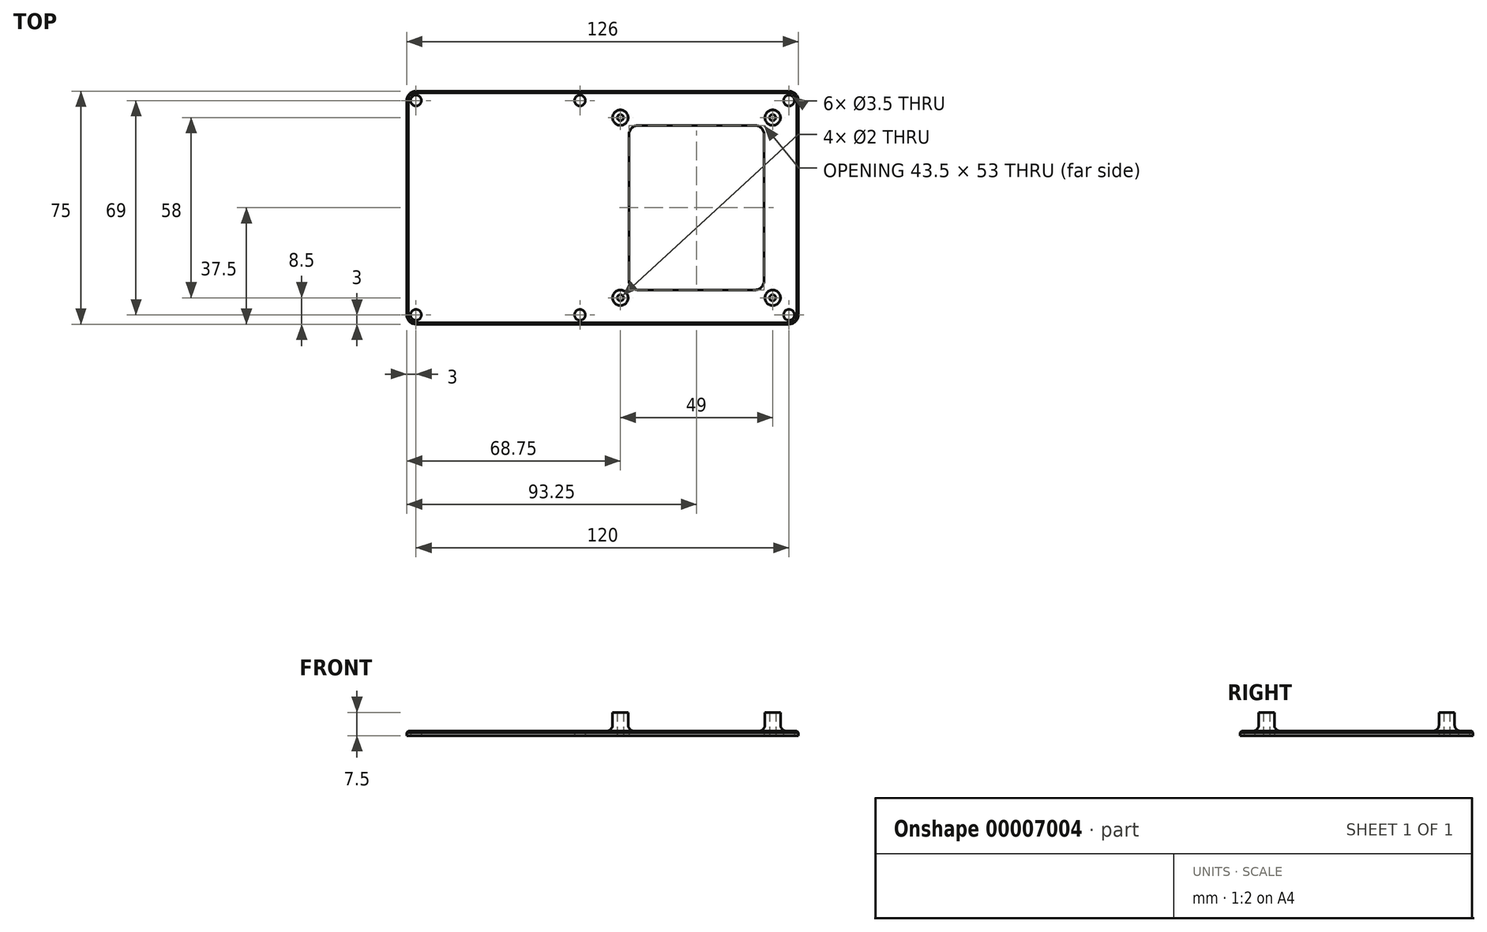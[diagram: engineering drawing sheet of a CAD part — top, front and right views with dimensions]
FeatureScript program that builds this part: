
annotation { "Feature Type Name" : "Feature", "Feature Type Description" : "" }
export const myFeature = defineFeature(function(context is Context, id is Id, definition is map)
    precondition{}
    {
        {
            var Q0;
            Q0=qCreatedBy(makeId("Top.planeOp"),FACE);
            var sketch = newSketch(context, id + "F0", { "sketchPlane" : qUnion([Q0])});
            skLineSegment(sketch, "E0", {"start": v(0, 0) * mm, "end": v(126, 0) * mm});
            skLineSegment(sketch, "E1", {"start": v(126, 0) * mm, "end": v(126, 75) * mm});
            skLineSegment(sketch, "E2", {"start": v(126, 75) * mm, "end": v(0, 75) * mm});
            skLineSegment(sketch, "E3", {"start": v(0, 75) * mm, "end": v(0, 0) * mm});
            skLineSegment(sketch, "E4", {"start": v(60.5, 75) * mm, "end": v(60.5, 0) * mm});
            skLineSegment(sketch, "E5.0", {"start": v(126, 64) * mm, "end": v(60.5, 64) * mm});
            skLineSegment(sketch, "E6.0", {"start": v(60.5, 11) * mm, "end": v(126, 11) * mm});
            skLineSegment(sketch, "E7.0", {"start": v(115, 0) * mm, "end": v(115, 75) * mm});
            skLineSegment(sketch, "E8", {"start": v(93.25, 75) * mm, "end": v(93.25, 0) * mm});
            skPoint(sketch, "E8.startSnap0", {"position": v(93.25, 64) * mm});
            skLineSegment(sketch, "E9", {"start": v(93.25, 37.5) * mm, "end": v(68.75, 37.5) * mm});
            skPoint(sketch, "E9.endSnap0", {"position": v(93.25, 37.5) * mm});
            skLineSegment(sketch, "E10", {"start": v(93.25, 37.5) * mm, "end": v(117.75, 37.5) * mm});
            skLineSegment(sketch, "E11", {"start": v(68.75, 37.5) * mm, "end": v(68.75, 66.5) * mm});
            skLineSegment(sketch, "E12", {"start": v(117.75, 37.5) * mm, "end": v(117.75, 8.5) * mm});
            skLineSegment(sketch, "E13.bottom", {"start": v(68.75, 66.5) * mm, "end": v(117.75, 66.5) * mm});
            skLineSegment(sketch, "E13.top", {"start": v(68.75, 8.5) * mm, "end": v(117.75, 8.5) * mm});
            skLineSegment(sketch, "E13.left", {"start": v(68.75, 66.5) * mm, "end": v(68.75, 8.5) * mm});
            skLineSegment(sketch, "E13.right", {"start": v(117.75, 66.5) * mm, "end": v(117.75, 8.5) * mm});
            skCircle(sketch, "E14", {"center": v(68.75, 8.5) * mm, "radius": 1 * mm});
            skCircle(sketch, "E15", {"center": v(117.75, 8.5) * mm, "radius": 1 * mm});
            skCircle(sketch, "E16", {"center": v(68.75, 66.5) * mm, "radius": 1 * mm});
            skCircle(sketch, "E17", {"center": v(117.75, 66.5) * mm, "radius": 1 * mm});
            skLineSegment(sketch, "E18.0", {"start": v(71.5, 75) * mm, "end": v(71.5, 0) * mm});
            skLineSegment(sketch, "E19", {"start": v(126, 37.5) * mm, "end": v(55.75, 37.5) * mm});
            skLineSegment(sketch, "E20", {"start": v(55.75, 37.5) * mm, "end": v(55.75, 72) * mm});
            skLineSegment(sketch, "E21", {"start": v(55.75, 37.5) * mm, "end": v(55.75, 3) * mm});
            skCircle(sketch, "E22", {"center": v(55.75, 3) * mm, "radius": 1.75 * mm});
            skCircle(sketch, "E23", {"center": v(55.75, 72) * mm, "radius": 1.75 * mm});
            skLineSegment(sketch, "E24.0", {"start": v(126, 72) * mm, "end": v(0, 72) * mm});
            skLineSegment(sketch, "E25.0", {"start": v(0, 3) * mm, "end": v(126, 3) * mm});
            skLineSegment(sketch, "E26.0", {"start": v(3, 75) * mm, "end": v(3, 0) * mm});
            skLineSegment(sketch, "E27.0", {"start": v(123, 0) * mm, "end": v(123, 75) * mm});
            skCircle(sketch, "E28", {"center": v(3, 3) * mm, "radius": 1.75 * mm});
            skCircle(sketch, "E29", {"center": v(123, 3) * mm, "radius": 1.75 * mm});
            skCircle(sketch, "E30", {"center": v(123, 72) * mm, "radius": 1.75 * mm});
            skCircle(sketch, "E31", {"center": v(3, 72) * mm, "radius": 1.75 * mm});
            skSolve(sketch);
        }
        {
            var Q0;
            Q0=qCreatedBy(makeId("Top.planeOp"),FACE);
            var sketch = newSketch(context, id + "F1", { "sketchPlane" : qUnion([Q0])});
            skLineSegment(sketch, "E32.0", {"start": v(0, 75) * mm, "end": v(0, 0) * mm});
            skLineSegment(sketch, "E32.1", {"start": v(126, 75) * mm, "end": v(0, 75) * mm});
            skLineSegment(sketch, "E32.2", {"start": v(126, 0) * mm, "end": v(126, 75) * mm});
            skLineSegment(sketch, "E32.3", {"start": v(0, 0) * mm, "end": v(126, 0) * mm});
            skCircle(sketch, "E32.4", {"center": v(55.75, 3) * mm, "radius": 1.75 * mm});
            skCircle(sketch, "E32.5", {"center": v(123, 3) * mm, "radius": 1.75 * mm});
            skCircle(sketch, "E32.6", {"center": v(55.75, 72) * mm, "radius": 1.75 * mm});
            skCircle(sketch, "E32.7", {"center": v(123, 72) * mm, "radius": 1.75 * mm});
            skLineSegment(sketch, "E32.8", {"start": v(115, 11) * mm, "end": v(115, 64) * mm});
            skLineSegment(sketch, "E32.9", {"start": v(115, 64) * mm, "end": v(71.5, 64) * mm});
            skLineSegment(sketch, "E32.10", {"start": v(71.5, 64) * mm, "end": v(71.5, 11) * mm});
            skLineSegment(sketch, "E32.11", {"start": v(71.5, 11) * mm, "end": v(115, 11) * mm});
            skCircle(sketch, "E32.12", {"center": v(3, 3) * mm, "radius": 1.75 * mm});
            skCircle(sketch, "E32.13", {"center": v(3, 72) * mm, "radius": 1.75 * mm});
            skPoint(sketch, "E33.orphan", {"position": v(60.5, 11) * mm});
            skPoint(sketch, "E34.orphan", {"position": v(71.5, 0) * mm});
            skPoint(sketch, "E35.orphan", {"position": v(60.5, 64) * mm});
            skPoint(sketch, "E36.orphan", {"position": v(71.5, 75) * mm});
            skPoint(sketch, "E37.orphan", {"position": v(115, 75) * mm});
            skPoint(sketch, "E38.orphan", {"position": v(126, 64) * mm});
            skPoint(sketch, "E39.orphan", {"position": v(126, 11) * mm});
            skPoint(sketch, "E40.orphan", {"position": v(115, 0) * mm});
            skSolve(sketch);
        }
        {
            var Q0;
            Q0 = qSketchRegion(id + "F1", true);
            extrude(context, id + "F2", {"entities" : qUnion([Q0]), "depth" : 1.5 * mm});
        }
        {
            var Q0;
            Q0=makeQuery(id+"F2.opExtrude","SWEPT_EDGE",EDGE,{"disambiguationData":[OSD([sQuery(id+"F1.wireOp",EDGE,"E32.0"),sQuery(id+"F1.wireOp",EDGE,"E32.3")])]});
            var Q1;
            Q1=makeQuery(id+"F2.opExtrude","SWEPT_EDGE",EDGE,{"disambiguationData":[OSD([sQuery(id+"F1.wireOp",EDGE,"E32.2"),sQuery(id+"F1.wireOp",EDGE,"E32.3")])]});
            var Q2;
            Q2=makeQuery(id+"F2.opExtrude","SWEPT_EDGE",EDGE,{"disambiguationData":[OSD([sQuery(id+"F1.wireOp",EDGE,"E32.0"),sQuery(id+"F1.wireOp",EDGE,"E32.1")])]});
            var Q3;
            Q3=makeQuery(id+"F2.opExtrude","SWEPT_EDGE",EDGE,{"disambiguationData":[OSD([sQuery(id+"F1.wireOp",EDGE,"E32.8"),sQuery(id+"F1.wireOp",EDGE,"E32.11")])]});
            var Q4;
            Q4=makeQuery(id+"F2.opExtrude","SWEPT_EDGE",EDGE,{"disambiguationData":[OSD([sQuery(id+"F1.wireOp",EDGE,"E32.9"),sQuery(id+"F1.wireOp",EDGE,"E32.10")])]});
            var Q5;
            Q5=makeQuery(id+"F2.opExtrude","SWEPT_EDGE",EDGE,{"disambiguationData":[OSD([sQuery(id+"F1.wireOp",EDGE,"E32.8"),sQuery(id+"F1.wireOp",EDGE,"E32.9")])]});
            var Q6;
            Q6=makeQuery(id+"F2.opExtrude","SWEPT_EDGE",EDGE,{"disambiguationData":[OSD([sQuery(id+"F1.wireOp",EDGE,"E32.1"),sQuery(id+"F1.wireOp",EDGE,"E32.2")])]});
            var Q7;
            Q7=makeQuery(id+"F2.opExtrude","SWEPT_EDGE",EDGE,{"disambiguationData":[OSD([sQuery(id+"F1.wireOp",EDGE,"E32.10"),sQuery(id+"F1.wireOp",EDGE,"E32.11")])]});
            fillet(context, id + "F3", {"entities" : qUnion([Q0, Q1, Q2, Q3, Q4, Q5, Q6, Q7]), "radius" : 3 * mm, "tangentPropagation" : true, "allowEdgeOverflow" : false});
        }
        {
            var Q0;
            Q0=qCreatedBy(makeId("Top.planeOp"),FACE);
            var sketch = newSketch(context, id + "F4", { "sketchPlane" : qUnion([Q0])});
            skCircle(sketch, "E41", {"center": v(68.75, 66.5) * mm, "radius": 2.5 * mm});
            skCircle(sketch, "E42", {"center": v(117.75, 66.5) * mm, "radius": 2.5 * mm});
            skCircle(sketch, "E43", {"center": v(68.75, 8.5) * mm, "radius": 2.5 * mm});
            skCircle(sketch, "E44", {"center": v(117.75, 8.5) * mm, "radius": 2.5 * mm});
            skSolve(sketch);
        }
        {
            var Q0;
            Q0 = qSketchRegion(id + "F4", true);
            extrude(context, id + "F5", {"entities" : qUnion([Q0]), "operationType" : NewBodyOperationType.ADD, "depth" : 7.5 * mm});
        }
        {
            var Q0;
            Q0=makeQuery(id+"F5.boolean.opBoolean","INTERSECT",EDGE,{"derivedFrom":[makeQuery(id+"F2.opExtrude","CAP_FACE",FACE,{"disambiguationData":[OSD([sQuery(id+"F1.wireOp",EDGE,"E32.0"),sQuery(id+"F1.wireOp",EDGE,"E32.1"),sQuery(id+"F1.wireOp",EDGE,"E32.2"),sQuery(id+"F1.wireOp",EDGE,"E32.3"),sQuery(id+"F1.wireOp",EDGE,"E32.4"),sQuery(id+"F1.wireOp",EDGE,"E32.5"),sQuery(id+"F1.wireOp",EDGE,"E32.6"),sQuery(id+"F1.wireOp",EDGE,"E32.7"),sQuery(id+"F1.wireOp",EDGE,"E32.8"),sQuery(id+"F1.wireOp",EDGE,"E32.9"),sQuery(id+"F1.wireOp",EDGE,"E32.10"),sQuery(id+"F1.wireOp",EDGE,"E32.11"),sQuery(id+"F1.wireOp",EDGE,"E32.12"),sQuery(id+"F1.wireOp",EDGE,"E32.13")])],"isStart":false}),makeQuery(id+"F5.opExtrude","SWEPT_FACE",FACE,{"disambiguationData":[OSD([sQuery(id+"F4.wireOp",EDGE,"E43")])]})]});
            var Q1;
            Q1=makeQuery(id+"F5.boolean.opBoolean","INTERSECT",EDGE,{"derivedFrom":[makeQuery(id+"F2.opExtrude","CAP_FACE",FACE,{"disambiguationData":[OSD([sQuery(id+"F1.wireOp",EDGE,"E32.0"),sQuery(id+"F1.wireOp",EDGE,"E32.1"),sQuery(id+"F1.wireOp",EDGE,"E32.2"),sQuery(id+"F1.wireOp",EDGE,"E32.3"),sQuery(id+"F1.wireOp",EDGE,"E32.4"),sQuery(id+"F1.wireOp",EDGE,"E32.5"),sQuery(id+"F1.wireOp",EDGE,"E32.6"),sQuery(id+"F1.wireOp",EDGE,"E32.7"),sQuery(id+"F1.wireOp",EDGE,"E32.8"),sQuery(id+"F1.wireOp",EDGE,"E32.9"),sQuery(id+"F1.wireOp",EDGE,"E32.10"),sQuery(id+"F1.wireOp",EDGE,"E32.11"),sQuery(id+"F1.wireOp",EDGE,"E32.12"),sQuery(id+"F1.wireOp",EDGE,"E32.13")])],"isStart":false}),makeQuery(id+"F5.opExtrude","SWEPT_FACE",FACE,{"disambiguationData":[OSD([sQuery(id+"F4.wireOp",EDGE,"E41")])]})]});
            var Q2;
            Q2=makeQuery(id+"F5.boolean.opBoolean","INTERSECT",EDGE,{"derivedFrom":[makeQuery(id+"F2.opExtrude","CAP_FACE",FACE,{"disambiguationData":[OSD([sQuery(id+"F1.wireOp",EDGE,"E32.0"),sQuery(id+"F1.wireOp",EDGE,"E32.1"),sQuery(id+"F1.wireOp",EDGE,"E32.2"),sQuery(id+"F1.wireOp",EDGE,"E32.3"),sQuery(id+"F1.wireOp",EDGE,"E32.4"),sQuery(id+"F1.wireOp",EDGE,"E32.5"),sQuery(id+"F1.wireOp",EDGE,"E32.6"),sQuery(id+"F1.wireOp",EDGE,"E32.7"),sQuery(id+"F1.wireOp",EDGE,"E32.8"),sQuery(id+"F1.wireOp",EDGE,"E32.9"),sQuery(id+"F1.wireOp",EDGE,"E32.10"),sQuery(id+"F1.wireOp",EDGE,"E32.11"),sQuery(id+"F1.wireOp",EDGE,"E32.12"),sQuery(id+"F1.wireOp",EDGE,"E32.13")])],"isStart":false}),makeQuery(id+"F5.opExtrude","SWEPT_FACE",FACE,{"disambiguationData":[OSD([sQuery(id+"F4.wireOp",EDGE,"E44")])]})]});
            var Q3;
            Q3=makeQuery(id+"F5.boolean.opBoolean","INTERSECT",EDGE,{"derivedFrom":[makeQuery(id+"F2.opExtrude","CAP_FACE",FACE,{"disambiguationData":[OSD([sQuery(id+"F1.wireOp",EDGE,"E32.0"),sQuery(id+"F1.wireOp",EDGE,"E32.1"),sQuery(id+"F1.wireOp",EDGE,"E32.2"),sQuery(id+"F1.wireOp",EDGE,"E32.3"),sQuery(id+"F1.wireOp",EDGE,"E32.4"),sQuery(id+"F1.wireOp",EDGE,"E32.5"),sQuery(id+"F1.wireOp",EDGE,"E32.6"),sQuery(id+"F1.wireOp",EDGE,"E32.7"),sQuery(id+"F1.wireOp",EDGE,"E32.8"),sQuery(id+"F1.wireOp",EDGE,"E32.9"),sQuery(id+"F1.wireOp",EDGE,"E32.10"),sQuery(id+"F1.wireOp",EDGE,"E32.11"),sQuery(id+"F1.wireOp",EDGE,"E32.12"),sQuery(id+"F1.wireOp",EDGE,"E32.13")])],"isStart":false}),makeQuery(id+"F5.opExtrude","SWEPT_FACE",FACE,{"disambiguationData":[OSD([sQuery(id+"F4.wireOp",EDGE,"E42")])]})]});
            fillet(context, id + "F6", {"entities" : qUnion([Q0, Q1, Q2, Q3]), "radius" : 2 * mm, "tangentPropagation" : true, "allowEdgeOverflow" : false});
        }
        {
            var Q0;
            {var subQ0=sQuery(id+"F0.wireOp",EDGE,"E13.left");var subQ1=sQuery(id+"F0.wireOp",EDGE,"E13.top");var subQ2=makeQuery(id+"F0.imprint","INTERSECT",VERTEX,{"derivedFrom":[subQ1,subQ0]});Q0=makeQuery(id+"F0.imprint","IMPRINT",FACE,{"disambiguationData":[TD([[makeQuery(id+"F0.imprint","IMPRINT",EDGE,{"disambiguationData":[TD([[subQ2,-1.0]])],"derivedFrom":subQ1}),-1.0]])]});}
            var Q1;
            {var subQ0=sQuery(id+"F0.wireOp",EDGE,"E13.left");var subQ1=sQuery(id+"F0.wireOp",EDGE,"E13.top");var subQ2=makeQuery(id+"F0.imprint","INTERSECT",VERTEX,{"derivedFrom":[subQ1,subQ0]});Q1=makeQuery(id+"F0.imprint","IMPRINT",FACE,{"disambiguationData":[TD([[makeQuery(id+"F0.imprint","IMPRINT",EDGE,{"disambiguationData":[TD([[subQ2,-1.0]])],"derivedFrom":subQ1}),1.0]])]});}
            var Q2;
            {var subQ0=sQuery(id+"F0.wireOp",EDGE,"E13.right");var subQ1=sQuery(id+"F0.wireOp",EDGE,"E13.top");var subQ2=makeQuery(id+"F0.imprint","INTERSECT",VERTEX,{"derivedFrom":[subQ1,subQ0]});Q2=makeQuery(id+"F0.imprint","IMPRINT",FACE,{"disambiguationData":[TD([[makeQuery(id+"F0.imprint","IMPRINT",EDGE,{"disambiguationData":[TD([[subQ2,1.0]])],"derivedFrom":subQ1}),-1.0]])]});}
            var Q3;
            {var subQ0=sQuery(id+"F0.wireOp",EDGE,"E13.right");var subQ1=sQuery(id+"F0.wireOp",EDGE,"E13.top");var subQ2=makeQuery(id+"F0.imprint","INTERSECT",VERTEX,{"derivedFrom":[subQ1,subQ0]});Q3=makeQuery(id+"F0.imprint","IMPRINT",FACE,{"disambiguationData":[TD([[makeQuery(id+"F0.imprint","IMPRINT",EDGE,{"disambiguationData":[TD([[subQ2,1.0]])],"derivedFrom":subQ1}),1.0]])]});}
            var Q4;
            {var subQ0=sQuery(id+"F0.wireOp",EDGE,"E13.right");var subQ1=sQuery(id+"F0.wireOp",EDGE,"E13.bottom");var subQ2=makeQuery(id+"F0.imprint","INTERSECT",VERTEX,{"derivedFrom":[subQ1,subQ0]});Q4=makeQuery(id+"F0.imprint","IMPRINT",FACE,{"disambiguationData":[TD([[makeQuery(id+"F0.imprint","IMPRINT",EDGE,{"disambiguationData":[TD([[subQ2,1.0]])],"derivedFrom":subQ1}),-1.0]])]});}
            var Q5;
            {var subQ0=sQuery(id+"F0.wireOp",EDGE,"E13.right");var subQ1=sQuery(id+"F0.wireOp",EDGE,"E13.bottom");var subQ2=makeQuery(id+"F0.imprint","INTERSECT",VERTEX,{"derivedFrom":[subQ1,subQ0]});Q5=makeQuery(id+"F0.imprint","IMPRINT",FACE,{"disambiguationData":[TD([[makeQuery(id+"F0.imprint","IMPRINT",EDGE,{"disambiguationData":[TD([[subQ2,1.0]])],"derivedFrom":subQ1}),1.0]])]});}
            var Q6;
            {var subQ0=sQuery(id+"F0.wireOp",EDGE,"E13.left");var subQ1=sQuery(id+"F0.wireOp",EDGE,"E13.bottom");var subQ2=makeQuery(id+"F0.imprint","INTERSECT",VERTEX,{"derivedFrom":[subQ1,subQ0]});Q6=makeQuery(id+"F0.imprint","IMPRINT",FACE,{"disambiguationData":[TD([[makeQuery(id+"F0.imprint","IMPRINT",EDGE,{"disambiguationData":[TD([[subQ2,-1.0]])],"derivedFrom":subQ1}),1.0]])]});}
            var Q7;
            {var subQ0=sQuery(id+"F0.wireOp",EDGE,"E13.left");var subQ1=sQuery(id+"F0.wireOp",EDGE,"E13.bottom");var subQ2=makeQuery(id+"F0.imprint","INTERSECT",VERTEX,{"derivedFrom":[subQ1,subQ0]});Q7=makeQuery(id+"F0.imprint","IMPRINT",FACE,{"disambiguationData":[TD([[makeQuery(id+"F0.imprint","IMPRINT",EDGE,{"disambiguationData":[TD([[subQ2,-1.0]])],"derivedFrom":subQ1}),-1.0]])]});}
            var Q8;
            Q8=sQuery(id+"F0.wireOp",EDGE,"E14");
            var Q9;
            Q9=sQuery(id+"F0.wireOp",EDGE,"E16");
            var Q10;
            Q10=sQuery(id+"F0.wireOp",EDGE,"E17");
            var Q11;
            Q11=sQuery(id+"F0.wireOp",EDGE,"E15");
            extrude(context, id + "F7", {"entities" : qUnion([Q0, Q1, Q2, Q3, Q4, Q5, Q6, Q7]), "operationType" : NewBodyOperationType.REMOVE, "surfaceEntities" : qUnion([Q8, Q9, Q10, Q11]), "depth" : 25 * mm});
        }
        {
            var Q0;
            Q0=makeQuery(id+"F2.opExtrude","CAP_EDGE",EDGE,{"disambiguationData":[OSD([sQuery(id+"F1.wireOp",EDGE,"E32.2")])],"isStart":false});
            var Q1;
            {var subQ0=sQuery(id+"F1.wireOp",EDGE,"E32.3");var subQ1=sQuery(id+"F1.wireOp",EDGE,"E32.2");Q1=makeQuery(id+"F3.opFillet","BLEND_EDGE",EDGE,{"blendedFrom":[makeQuery(id+"F2.opExtrude","SWEPT_EDGE",EDGE,{"disambiguationData":[OSD([subQ1,subQ0])]}),makeQuery(id+"F2.opExtrude","CAP_FACE",FACE,{"disambiguationData":[OSD([sQuery(id+"F1.wireOp",EDGE,"E32.0"),sQuery(id+"F1.wireOp",EDGE,"E32.1"),subQ1,subQ0,sQuery(id+"F1.wireOp",EDGE,"E32.4"),sQuery(id+"F1.wireOp",EDGE,"E32.5"),sQuery(id+"F1.wireOp",EDGE,"E32.6"),sQuery(id+"F1.wireOp",EDGE,"E32.7"),sQuery(id+"F1.wireOp",EDGE,"E32.8"),sQuery(id+"F1.wireOp",EDGE,"E32.9"),sQuery(id+"F1.wireOp",EDGE,"E32.10"),sQuery(id+"F1.wireOp",EDGE,"E32.11"),sQuery(id+"F1.wireOp",EDGE,"E32.12"),sQuery(id+"F1.wireOp",EDGE,"E32.13")])],"isStart":false})],"blendedInto":[makeQuery(id+"F2.opExtrude","CAP_FACE",FACE,{"disambiguationData":[OSD([sQuery(id+"F1.wireOp",EDGE,"E32.0"),sQuery(id+"F1.wireOp",EDGE,"E32.1"),subQ1,subQ0,sQuery(id+"F1.wireOp",EDGE,"E32.4"),sQuery(id+"F1.wireOp",EDGE,"E32.5"),sQuery(id+"F1.wireOp",EDGE,"E32.6"),sQuery(id+"F1.wireOp",EDGE,"E32.7"),sQuery(id+"F1.wireOp",EDGE,"E32.8"),sQuery(id+"F1.wireOp",EDGE,"E32.9"),sQuery(id+"F1.wireOp",EDGE,"E32.10"),sQuery(id+"F1.wireOp",EDGE,"E32.11"),sQuery(id+"F1.wireOp",EDGE,"E32.12"),sQuery(id+"F1.wireOp",EDGE,"E32.13")])],"isStart":false})]});}
            var Q2;
            Q2=makeQuery(id+"F2.opExtrude","CAP_EDGE",EDGE,{"disambiguationData":[OSD([sQuery(id+"F1.wireOp",EDGE,"E32.3")])],"isStart":false});
            var Q3;
            {var subQ0=sQuery(id+"F1.wireOp",EDGE,"E32.2");var subQ1=sQuery(id+"F1.wireOp",EDGE,"E32.1");Q3=makeQuery(id+"F3.opFillet","BLEND_EDGE",EDGE,{"blendedFrom":[makeQuery(id+"F2.opExtrude","SWEPT_EDGE",EDGE,{"disambiguationData":[OSD([subQ1,subQ0])]}),makeQuery(id+"F2.opExtrude","CAP_FACE",FACE,{"disambiguationData":[OSD([sQuery(id+"F1.wireOp",EDGE,"E32.0"),subQ1,subQ0,sQuery(id+"F1.wireOp",EDGE,"E32.3"),sQuery(id+"F1.wireOp",EDGE,"E32.4"),sQuery(id+"F1.wireOp",EDGE,"E32.5"),sQuery(id+"F1.wireOp",EDGE,"E32.6"),sQuery(id+"F1.wireOp",EDGE,"E32.7"),sQuery(id+"F1.wireOp",EDGE,"E32.8"),sQuery(id+"F1.wireOp",EDGE,"E32.9"),sQuery(id+"F1.wireOp",EDGE,"E32.10"),sQuery(id+"F1.wireOp",EDGE,"E32.11"),sQuery(id+"F1.wireOp",EDGE,"E32.12"),sQuery(id+"F1.wireOp",EDGE,"E32.13")])],"isStart":false})],"blendedInto":[makeQuery(id+"F2.opExtrude","CAP_FACE",FACE,{"disambiguationData":[OSD([sQuery(id+"F1.wireOp",EDGE,"E32.0"),subQ1,subQ0,sQuery(id+"F1.wireOp",EDGE,"E32.3"),sQuery(id+"F1.wireOp",EDGE,"E32.4"),sQuery(id+"F1.wireOp",EDGE,"E32.5"),sQuery(id+"F1.wireOp",EDGE,"E32.6"),sQuery(id+"F1.wireOp",EDGE,"E32.7"),sQuery(id+"F1.wireOp",EDGE,"E32.8"),sQuery(id+"F1.wireOp",EDGE,"E32.9"),sQuery(id+"F1.wireOp",EDGE,"E32.10"),sQuery(id+"F1.wireOp",EDGE,"E32.11"),sQuery(id+"F1.wireOp",EDGE,"E32.12"),sQuery(id+"F1.wireOp",EDGE,"E32.13")])],"isStart":false})]});}
            var Q4;
            Q4=makeQuery(id+"F2.opExtrude","CAP_EDGE",EDGE,{"disambiguationData":[OSD([sQuery(id+"F1.wireOp",EDGE,"E32.1")])],"isStart":false});
            var Q5;
            {var subQ0=sQuery(id+"F1.wireOp",EDGE,"E32.3");var subQ1=sQuery(id+"F1.wireOp",EDGE,"E32.0");Q5=makeQuery(id+"F3.opFillet","BLEND_EDGE",EDGE,{"blendedFrom":[makeQuery(id+"F2.opExtrude","SWEPT_EDGE",EDGE,{"disambiguationData":[OSD([subQ1,subQ0])]}),makeQuery(id+"F2.opExtrude","CAP_FACE",FACE,{"disambiguationData":[OSD([subQ1,sQuery(id+"F1.wireOp",EDGE,"E32.1"),sQuery(id+"F1.wireOp",EDGE,"E32.2"),subQ0,sQuery(id+"F1.wireOp",EDGE,"E32.4"),sQuery(id+"F1.wireOp",EDGE,"E32.5"),sQuery(id+"F1.wireOp",EDGE,"E32.6"),sQuery(id+"F1.wireOp",EDGE,"E32.7"),sQuery(id+"F1.wireOp",EDGE,"E32.8"),sQuery(id+"F1.wireOp",EDGE,"E32.9"),sQuery(id+"F1.wireOp",EDGE,"E32.10"),sQuery(id+"F1.wireOp",EDGE,"E32.11"),sQuery(id+"F1.wireOp",EDGE,"E32.12"),sQuery(id+"F1.wireOp",EDGE,"E32.13")])],"isStart":false})],"blendedInto":[makeQuery(id+"F2.opExtrude","CAP_FACE",FACE,{"disambiguationData":[OSD([subQ1,sQuery(id+"F1.wireOp",EDGE,"E32.1"),sQuery(id+"F1.wireOp",EDGE,"E32.2"),subQ0,sQuery(id+"F1.wireOp",EDGE,"E32.4"),sQuery(id+"F1.wireOp",EDGE,"E32.5"),sQuery(id+"F1.wireOp",EDGE,"E32.6"),sQuery(id+"F1.wireOp",EDGE,"E32.7"),sQuery(id+"F1.wireOp",EDGE,"E32.8"),sQuery(id+"F1.wireOp",EDGE,"E32.9"),sQuery(id+"F1.wireOp",EDGE,"E32.10"),sQuery(id+"F1.wireOp",EDGE,"E32.11"),sQuery(id+"F1.wireOp",EDGE,"E32.12"),sQuery(id+"F1.wireOp",EDGE,"E32.13")])],"isStart":false})]});}
            var Q6;
            Q6=makeQuery(id+"F2.opExtrude","CAP_EDGE",EDGE,{"disambiguationData":[OSD([sQuery(id+"F1.wireOp",EDGE,"E32.0")])],"isStart":false});
            var Q7;
            {var subQ0=sQuery(id+"F1.wireOp",EDGE,"E32.1");var subQ1=sQuery(id+"F1.wireOp",EDGE,"E32.0");Q7=makeQuery(id+"F3.opFillet","BLEND_EDGE",EDGE,{"blendedFrom":[makeQuery(id+"F2.opExtrude","SWEPT_EDGE",EDGE,{"disambiguationData":[OSD([subQ1,subQ0])]}),makeQuery(id+"F2.opExtrude","CAP_FACE",FACE,{"disambiguationData":[OSD([subQ1,subQ0,sQuery(id+"F1.wireOp",EDGE,"E32.2"),sQuery(id+"F1.wireOp",EDGE,"E32.3"),sQuery(id+"F1.wireOp",EDGE,"E32.4"),sQuery(id+"F1.wireOp",EDGE,"E32.5"),sQuery(id+"F1.wireOp",EDGE,"E32.6"),sQuery(id+"F1.wireOp",EDGE,"E32.7"),sQuery(id+"F1.wireOp",EDGE,"E32.8"),sQuery(id+"F1.wireOp",EDGE,"E32.9"),sQuery(id+"F1.wireOp",EDGE,"E32.10"),sQuery(id+"F1.wireOp",EDGE,"E32.11"),sQuery(id+"F1.wireOp",EDGE,"E32.12"),sQuery(id+"F1.wireOp",EDGE,"E32.13")])],"isStart":false})],"blendedInto":[makeQuery(id+"F2.opExtrude","CAP_FACE",FACE,{"disambiguationData":[OSD([subQ1,subQ0,sQuery(id+"F1.wireOp",EDGE,"E32.2"),sQuery(id+"F1.wireOp",EDGE,"E32.3"),sQuery(id+"F1.wireOp",EDGE,"E32.4"),sQuery(id+"F1.wireOp",EDGE,"E32.5"),sQuery(id+"F1.wireOp",EDGE,"E32.6"),sQuery(id+"F1.wireOp",EDGE,"E32.7"),sQuery(id+"F1.wireOp",EDGE,"E32.8"),sQuery(id+"F1.wireOp",EDGE,"E32.9"),sQuery(id+"F1.wireOp",EDGE,"E32.10"),sQuery(id+"F1.wireOp",EDGE,"E32.11"),sQuery(id+"F1.wireOp",EDGE,"E32.12"),sQuery(id+"F1.wireOp",EDGE,"E32.13")])],"isStart":false})]});}
            chamfer(context, id + "F8", {"entities" : qUnion([Q0, Q1, Q2, Q3, Q4, Q5, Q6, Q7]), "width" : .5 * mm, "tangentPropagation" : true});
        }
    });
